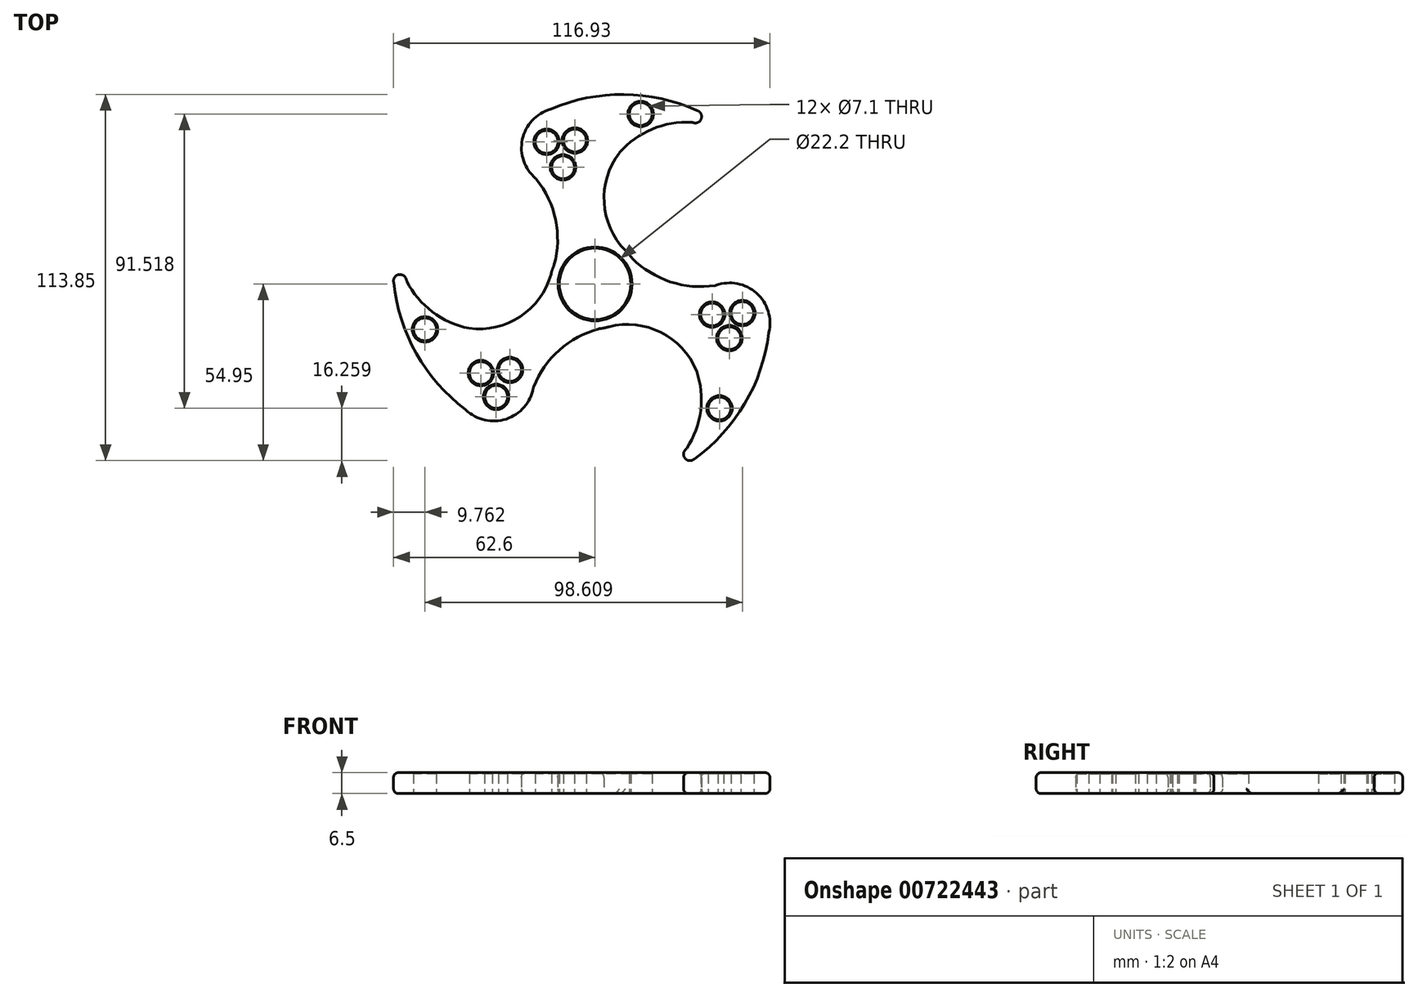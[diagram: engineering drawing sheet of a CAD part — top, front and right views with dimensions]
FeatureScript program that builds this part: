
annotation { "Feature Type Name" : "Feature", "Feature Type Description" : "" }
export const myFeature = defineFeature(function(context is Context, id is Id, definition is map)
    precondition{}
    {
        {
            var Q0;
            Q0=qCreatedBy(makeId("Top.planeOp"),FACE);
            var sketch = newSketch(context, id + "F0", { "sketchPlane" : qUnion([Q0])});
            skCircle(sketch, "E0", {"center": v(0, 0) * mm, "radius": 11.1 * mm});
            skCircle(sketch, "E1", {"center": v(0, 0) * mm, "radius": 14 * mm});
            skArc(sketch, "E2", {"start": v(-12.7, 5.88) * mm, "mid": v(-12.7, 21.7) * mm, "end": v(-20.72, 35.32) * mm});
            skCircle(sketch, "E3", {"center": v(-10.36, 42.32) * mm, "radius": 12.5 * mm});
            skPoint(sketch, "E3.second.point", {"position": v(0, 49.31) * mm});
            skPoint(sketch, "E3.third.point", {"position": v(0, 35.32) * mm});
            skArc(sketch, "E4", {"start": v(-13.78, 54.34) * mm, "mid": v(9.27, 58.9) * mm, "end": v(32.18, 53.7) * mm});
            skCircle(sketch, "E5", {"center": v(31.11, 52.02) * mm, "radius": 2 * mm});
            skPoint(sketch, "E5.second.point", {"position": v(30.27, 50.2) * mm});
            skPoint(sketch, "E5.third.point", {"position": v(29.7, 50.61) * mm});
            skArc(sketch, "E6", {"start": v(30.27, 50.2) * mm, "mid": v(17.83, 48.17) * mm, "end": v(7.61, 40.79) * mm});
            skArc(sketch, "E7", {"start": v(7.61, 40.79) * mm, "mid": v(2.86, 24.76) * mm, "end": v(10.1, 9.7) * mm});
            skArc(sketch, "E8.1.0", {"start": v(-40.17, -39.1) * mm, "mid": v(-55.64, -21.42) * mm, "end": v(-62.6, 1.01) * mm});
            skArc(sketch, "E8.2.0", {"start": v(53.95, -15.24) * mm, "mid": v(46.37, -37.47) * mm, "end": v(30.42, -54.72) * mm});
            skArc(sketch, "E9.1.0", {"start": v(-58.62, 1.11) * mm, "mid": v(-50.63, -8.64) * mm, "end": v(-39.13, -13.8) * mm});
            skArc(sketch, "E9.2.0", {"start": v(28.35, -51.32) * mm, "mid": v(32.8, -39.53) * mm, "end": v(31.52, -26.99) * mm});
            skCircle(sketch, "E10.1.0", {"center": v(-60.6, 0.94) * mm, "radius": 2 * mm});
            skCircle(sketch, "E10.2.0", {"center": v(29.5, -52.96) * mm, "radius": 2 * mm});
            skArc(sketch, "E11.1.0", {"start": v(1.26, -13.94) * mm, "mid": v(-12.44, -21.84) * mm, "end": v(-20.23, -35.6) * mm});
            skArc(sketch, "E11.2.0", {"start": v(11.45, 8.06) * mm, "mid": v(25.14, 0.14) * mm, "end": v(40.95, 0.28) * mm});
            skArc(sketch, "E12.1.0", {"start": v(-39.13, -13.8) * mm, "mid": v(-22.88, -9.9) * mm, "end": v(-13.45, 3.9) * mm});
            skArc(sketch, "E12.2.0", {"start": v(31.52, -26.99) * mm, "mid": v(20.01, -14.86) * mm, "end": v(3.35, -13.6) * mm});
            skCircle(sketch, "E13.1.0", {"center": v(-31.47, -30.13) * mm, "radius": 12.5 * mm});
            skCircle(sketch, "E13.2.0", {"center": v(41.83, -12.19) * mm, "radius": 12.5 * mm});
            skCircle(sketch, "E14", {"center": v(-6.27, 44.57) * mm, "radius": 3.55 * mm});
            skCircle(sketch, "E15", {"center": v(14.18, 52.83) * mm, "radius": 3.55 * mm});
            skCircle(sketch, "E16", {"center": v(-15.05, 44.16) * mm, "radius": 3.55 * mm});
            skCircle(sketch, "E17", {"center": v(-9.94, 36.25) * mm, "radius": 3.55 * mm});
            skCircle(sketch, "E18.1.0", {"center": v(-30.72, -35.11) * mm, "radius": 3.55 * mm});
            skCircle(sketch, "E18.2.0", {"center": v(45.77, -9.05) * mm, "radius": 3.55 * mm});
            skCircle(sketch, "E19.1.0", {"center": v(-35.47, -27.71) * mm, "radius": 3.55 * mm});
            skCircle(sketch, "E19.2.0", {"center": v(41.73, -16.86) * mm, "radius": 3.55 * mm});
            skCircle(sketch, "E20.1.0", {"center": v(-26.42, -26.74) * mm, "radius": 3.55 * mm});
            skCircle(sketch, "E20.2.0", {"center": v(36.36, -9.51) * mm, "radius": 3.55 * mm});
            skCircle(sketch, "E21.1.0", {"center": v(-52.84, -14.14) * mm, "radius": 3.55 * mm});
            skCircle(sketch, "E21.2.0", {"center": v(38.66, -38.7) * mm, "radius": 3.55 * mm});
            skSolve(sketch);
        }
        {
            var Q0;
            Q0 = qSketchRegion(id + "F0", true);
            extrude(context, id + "F1", {"entities" : qUnion([Q0]), "depth" : 6.5 * mm, "offsetDistance" : 25 * mm});
        }
        {
            var Q0;
            Q0=makeQuery(id+"F1.opExtrude","SWEPT_FACE",FACE,{"disambiguationData":[OSD([sQuery(id+"F0.wireOp",EDGE,"E4")])]});
            var Q1;
            Q1=makeQuery(id+"F1.opExtrude","SWEPT_FACE",FACE,{"disambiguationData":[OSD([sQuery(id+"F0.wireOp",EDGE,"E5")])]});
            var Q2;
            Q2=makeQuery(id+"F1.opExtrude","SWEPT_FACE",FACE,{"disambiguationData":[OSD([sQuery(id+"F0.wireOp",EDGE,"E6")])]});
            var Q3;
            Q3=makeQuery(id+"F1.opExtrude","CAP_EDGE",EDGE,{"disambiguationData":[OSD([sQuery(id+"F0.wireOp",EDGE,"E7")])],"isStart":false});
            var Q4;
            Q4=makeQuery(id+"F1.opExtrude","SWEPT_EDGE",EDGE,{"disambiguationData":[OSD([sQuery(id+"F0.wireOp",EDGE,"E1"),sQuery(id+"F0.wireOp",EDGE,"E11.2.0")])]});
            var Q5;
            {var subQ0=sQuery(id+"F0.wireOp",EDGE,"E7");var subQ1=sQuery(id+"F0.wireOp",EDGE,"E1");var subQ2=makeQuery(id+"F0.imprint","INTERSECT",VERTEX,{"disambiguationData":[OD(0.0)],"derivedFrom":[subQ1,subQ0]});Q5=makeQuery(id+"F1.opExtrude","SWEPT_FACE",FACE,{"disambiguationData":[OSD([subQ1]),TDD([makeQuery(id+"F0.imprint","IMPRINT",EDGE,{"disambiguationData":[TD([[subQ2,1.0]])],"derivedFrom":subQ1}),makeQuery(id+"F0.imprint","IMPRINT",EDGE,{"disambiguationData":[TD([[subQ2,-1.0]])],"derivedFrom":subQ1})])]});}
            var Q6;
            Q6=makeQuery(id+"F1.opExtrude","SWEPT_FACE",FACE,{"disambiguationData":[OSD([sQuery(id+"F0.wireOp",EDGE,"E11.2.0")])]});
            var Q7;
            Q7=makeQuery(id+"F1.opExtrude","SWEPT_FACE",FACE,{"disambiguationData":[OSD([sQuery(id+"F0.wireOp",EDGE,"E13.2.0")])]});
            var Q8;
            Q8=makeQuery(id+"F1.opExtrude","SWEPT_FACE",FACE,{"disambiguationData":[OSD([sQuery(id+"F0.wireOp",EDGE,"E8.2.0")])]});
            var Q9;
            Q9=makeQuery(id+"F1.opExtrude","SWEPT_FACE",FACE,{"disambiguationData":[OSD([sQuery(id+"F0.wireOp",EDGE,"E10.2.0")])]});
            var Q10;
            Q10=makeQuery(id+"F1.opExtrude","SWEPT_FACE",FACE,{"disambiguationData":[OSD([sQuery(id+"F0.wireOp",EDGE,"E9.2.0")])]});
            var Q11;
            Q11=makeQuery(id+"F1.opExtrude","SWEPT_FACE",FACE,{"disambiguationData":[OSD([sQuery(id+"F0.wireOp",EDGE,"E12.2.0")])]});
            var Q12;
            Q12=makeQuery(id+"F1.opExtrude","SWEPT_FACE",FACE,{"disambiguationData":[OSD([sQuery(id+"F0.wireOp",EDGE,"E11.1.0")])]});
            var Q13;
            {var subQ0=sQuery(id+"F0.wireOp",EDGE,"E12.2.0");var subQ1=sQuery(id+"F0.wireOp",EDGE,"E1");var subQ2=makeQuery(id+"F0.imprint","INTERSECT",VERTEX,{"disambiguationData":[OD(0.0)],"derivedFrom":[subQ1,subQ0]});Q13=makeQuery(id+"F1.opExtrude","SWEPT_FACE",FACE,{"disambiguationData":[OSD([subQ1]),TDD([makeQuery(id+"F0.imprint","IMPRINT",EDGE,{"disambiguationData":[TD([[makeQuery(id+"F0.imprint","INTERSECT",VERTEX,{"derivedFrom":[subQ1,sQuery(id+"F0.wireOp",EDGE,"E11.1.0")]}),-1.0]])],"derivedFrom":subQ1}),makeQuery(id+"F0.imprint","IMPRINT",EDGE,{"disambiguationData":[TD([[subQ2,-1.0]])],"derivedFrom":subQ1})])]});}
            var Q14;
            Q14=makeQuery(id+"F1.opExtrude","SWEPT_FACE",FACE,{"disambiguationData":[OSD([sQuery(id+"F0.wireOp",EDGE,"E13.1.0")])]});
            var Q15;
            Q15=makeQuery(id+"F1.opExtrude","SWEPT_FACE",FACE,{"disambiguationData":[OSD([sQuery(id+"F0.wireOp",EDGE,"E8.1.0")])]});
            var Q16;
            Q16=makeQuery(id+"F1.opExtrude","SWEPT_FACE",FACE,{"disambiguationData":[OSD([sQuery(id+"F0.wireOp",EDGE,"E12.1.0")])]});
            var Q17;
            Q17=makeQuery(id+"F1.opExtrude","SWEPT_FACE",FACE,{"disambiguationData":[OSD([sQuery(id+"F0.wireOp",EDGE,"E9.1.0")])]});
            var Q18;
            Q18=makeQuery(id+"F1.opExtrude","SWEPT_FACE",FACE,{"disambiguationData":[OSD([sQuery(id+"F0.wireOp",EDGE,"E10.1.0")])]});
            var Q19;
            Q19=makeQuery(id+"F1.opExtrude","SWEPT_FACE",FACE,{"disambiguationData":[OSD([sQuery(id+"F0.wireOp",EDGE,"E3")])]});
            var Q20;
            Q20=makeQuery(id+"F1.opExtrude","SWEPT_FACE",FACE,{"disambiguationData":[OSD([sQuery(id+"F0.wireOp",EDGE,"E2")])]});
            var Q21;
            {var subQ0=sQuery(id+"F0.wireOp",EDGE,"E12.1.0");var subQ1=sQuery(id+"F0.wireOp",EDGE,"E1");var subQ2=makeQuery(id+"F0.imprint","INTERSECT",VERTEX,{"disambiguationData":[OD(0.0)],"derivedFrom":[subQ1,subQ0]});Q21=makeQuery(id+"F1.opExtrude","SWEPT_FACE",FACE,{"disambiguationData":[OSD([subQ1]),TDD([makeQuery(id+"F0.imprint","IMPRINT",EDGE,{"disambiguationData":[TD([[makeQuery(id+"F0.imprint","INTERSECT",VERTEX,{"derivedFrom":[subQ1,sQuery(id+"F0.wireOp",EDGE,"E2")]}),-1.0]])],"derivedFrom":subQ1}),makeQuery(id+"F0.imprint","IMPRINT",EDGE,{"disambiguationData":[TD([[subQ2,-1.0]])],"derivedFrom":subQ1})])]});}
            fillet(context, id + "F2", {"entities" : qUnion([Q0, Q1, Q2, Q3, Q4, Q5, Q6, Q7, Q8, Q9, Q10, Q11, Q12, Q13, Q14, Q15, Q16, Q17, Q18, Q19, Q20, Q21]), "radius" : 1.5 * mm, "tangentPropagation" : true, "allowEdgeOverflow" : false});
        }
        {
            var Q0;
            Q0=makeQuery(id+"F1.opExtrude","CAP_EDGE",EDGE,{"disambiguationData":[OSD([sQuery(id+"F0.wireOp",EDGE,"E15")])],"isStart":false});
            var Q1;
            Q1=makeQuery(id+"F1.opExtrude","CAP_EDGE",EDGE,{"disambiguationData":[OSD([sQuery(id+"F0.wireOp",EDGE,"E14")])],"isStart":false});
            var Q2;
            Q2=makeQuery(id+"F1.opExtrude","CAP_EDGE",EDGE,{"disambiguationData":[OSD([sQuery(id+"F0.wireOp",EDGE,"E16")])],"isStart":false});
            var Q3;
            Q3=makeQuery(id+"F1.opExtrude","CAP_EDGE",EDGE,{"disambiguationData":[OSD([sQuery(id+"F0.wireOp",EDGE,"E17")])],"isStart":false});
            var Q4;
            Q4=makeQuery(id+"F1.opExtrude","CAP_EDGE",EDGE,{"disambiguationData":[OSD([sQuery(id+"F0.wireOp",EDGE,"E0")])],"isStart":false});
            var Q5;
            Q5=makeQuery(id+"F1.opExtrude","CAP_EDGE",EDGE,{"disambiguationData":[OSD([sQuery(id+"F0.wireOp",EDGE,"E20.2.0")])],"isStart":false});
            var Q6;
            Q6=makeQuery(id+"F1.opExtrude","CAP_EDGE",EDGE,{"disambiguationData":[OSD([sQuery(id+"F0.wireOp",EDGE,"E18.2.0")])],"isStart":false});
            var Q7;
            Q7=makeQuery(id+"F1.opExtrude","CAP_EDGE",EDGE,{"disambiguationData":[OSD([sQuery(id+"F0.wireOp",EDGE,"E19.2.0")])],"isStart":false});
            var Q8;
            Q8=makeQuery(id+"F1.opExtrude","CAP_EDGE",EDGE,{"disambiguationData":[OSD([sQuery(id+"F0.wireOp",EDGE,"E21.2.0")])],"isStart":false});
            var Q9;
            Q9=makeQuery(id+"F1.opExtrude","CAP_EDGE",EDGE,{"disambiguationData":[OSD([sQuery(id+"F0.wireOp",EDGE,"E20.1.0")])],"isStart":false});
            var Q10;
            Q10=makeQuery(id+"F1.opExtrude","CAP_EDGE",EDGE,{"disambiguationData":[OSD([sQuery(id+"F0.wireOp",EDGE,"E19.1.0")])],"isStart":false});
            var Q11;
            Q11=makeQuery(id+"F1.opExtrude","CAP_EDGE",EDGE,{"disambiguationData":[OSD([sQuery(id+"F0.wireOp",EDGE,"E18.1.0")])],"isStart":false});
            var Q12;
            Q12=makeQuery(id+"F1.opExtrude","CAP_EDGE",EDGE,{"disambiguationData":[OSD([sQuery(id+"F0.wireOp",EDGE,"E21.1.0")])],"isStart":false});
            chamfer(context, id + "F3", {"entities" : qUnion([Q0, Q1, Q2, Q3, Q4, Q5, Q6, Q7, Q8, Q9, Q10, Q11, Q12]), "width" : 0.4 * mm, "tangentPropagation" : true});
        }
    });
